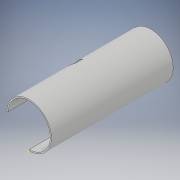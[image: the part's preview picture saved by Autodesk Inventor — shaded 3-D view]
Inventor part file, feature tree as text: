
AUTODESK INVENTOR PART (.ipt)
format: ipt  version: 2017 (Build 210142000, 142)  size: 192,000 bytes
history: native  units: in
note: dims shown in document units (in); Inventor stores cm internally (conversion verified against a paired STEP export)
features: sketch x12, extrude x5, plane x3, hole x1, mirror x1, other x1
ambient origin geometry x8: Origin, YZ Plane, XZ Plane, XY Plane, X Axis, Y Axis, Z Axis, Center Point
bodies: Solid1 (feature_tree)
feature tree (23):
  sketch  "Sketch1"  dims[d16=2.1654in d17=2.0472in]
  extrude  "Extrusion1"  Depth=2.0472in
  sketch  "Sketch3"  dims[d22=11.811in d23=0.0in d25=0.0481in]
  sketch  "Sketch4"  dims[d26=5.9055in d27=2.2441in]
  sketch  "Sketch5"  dims[d28=1.3386in d29=0.2644in]
  plane  "Work Plane1"
  hole  "Hole1"  [1 undecoded]
  extrude  "Extrusion2"  Depth=0.0481in
  sketch  "Sketch8"  dims[d39=0.5906in]
  sketch  "Sketch9"  dims[d41=1.2992in]
  plane  "Work Plane2"
  extrude  "Extrusion3"  Depth=2.2441in
  extrude  "Extrusion4"  Depth=0.2644in
  plane  "Work Plane3"
  mirror  "Mirror1"
  extrude  "Extrusion5"  Depth=1.9685in
  sketch  "Sketch2"  dims[d18=0.0in d20=2.8346in]
  other  "Work Point1"
  sketch  "Sketch6"  dims[d30=0.2644in]
  sketch  "Sketch7"  dims[d31=0.1732in d32=0.2362in d33=0.1575in d34=0.0787in d35=90.0deg d36=0.315in d37=0.8108in d38=1.9685in]
  sketch  "Sketch10"  dims[d42=0.3937in d43=0.0in]
  sketch  "Sketch12"  dims[d44=0.3937in d45=0.0in]
  sketch  "Sketch13"  dims[d47=2.0472in d48=2.1654in d49=15.0deg d50=1.7717in d51=0.0in d52=0.1718in d53=1.1811in d54=0.0in]
note: 1 required parameter value undecoded (feature->parameter linkage not recoverable at this tier; creation-order binding heuristic only, values carry confidence <= 0.55)
